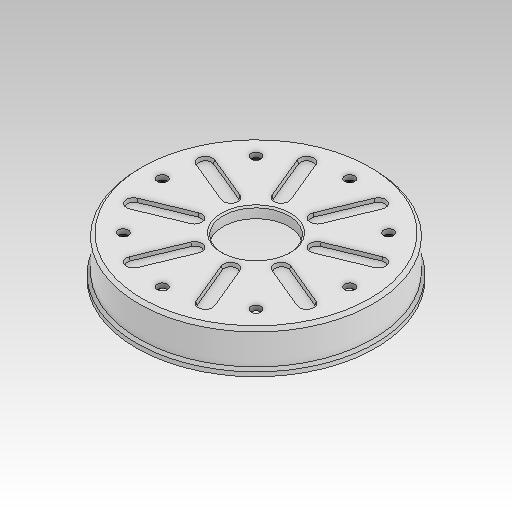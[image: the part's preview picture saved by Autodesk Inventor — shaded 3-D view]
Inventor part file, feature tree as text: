
AUTODESK INVENTOR PART (.ipt)
format: ipt  version: 2020 (Build 240168000, 168)  size: 1,618,944 bytes
history: native  units: mm
features: other x11, extrude x6, sketch x6, pattern_circular x4, chamfer x2, fillet x2, revolve x1, imported_body x1
ambient origin geometry x8: Origin, YZ Plane, XZ Plane, XY Plane, X Axis, Y Axis, Z Axis, Center Point
bodies: Solid1 (feature_tree)
feature tree (33):
  other  "HD_mastersketch.ipt"
  other  "Blocks"
  revolve  "Revolution1"  [1 undecoded]
  extrude  "Extrusion1"  Depth=4.0mm TaperAngle=0.0deg
  extrude  "Extrusion3"  Depth=1.7mm
  pattern_circular  "Circular Pattern1"  Count=73 Angle=360.0deg
  chamfer  "Chamfer1"  Distance=3.2mm
  extrude  "Extrusion2"  Depth=1.0mm
  fillet  "Fillet1"  Radius=4.0mm
  pattern_circular  "Circular Pattern2"  Angle=45.0deg  [1 undecoded]
  extrude  "Extrusion5"  Depth=10.0mm TaperAngle=0.0deg
  fillet  "Fillet2"  Radius=0.5mm
  pattern_circular  "Circular Pattern3"  Count=68 Angle=360.0deg
  extrude  "Extrusion6"  Depth=1.0mm
  chamfer  "Chamfer2"  Distance=22.5mm
  pattern_circular  "Circular Pattern4"  [2 undecoded]
  extrude  "Extrusion7"  Depth=1.0mm TaperAngle=0.0deg
  other  "608 bearing"
  other  "Belt"
  other  "Rotor"
  imported_body  "Base"
  sketch  "Sketch5"  dims[d0=10.0mm d24=7.0mm d25=22.0mm d26=8.0mm]
  sketch  "Sketch6"  dims[d1=90.0deg d4=4.0mm d5=0.0mm]
  sketch  "Sketch7"  dims[d6=80.0mm d7=360.0deg d9=1.7mm]
  other  "M3NutDepth_bot"
  other  "BeltCutDepth_bot"
  other  "M3NutDepth_top"
  other  "BeltCutDepth_top"
  sketch  "Sketch10"  dims[d11=1.25mm]
  sketch  "Sketch11"  dims[d12=4.0mm d13=0.0mm]
  sketch  "Sketch12"  dims[d14=0.5mm d15=730.0mm d16=360.0deg d18=3.2mm d19=5.7mm d20=4.0mm d21=0.0mm d34=0.5mm d35=2.0mm d36=45.0deg d37=0.8mm d38=1.8mm d39=8.726646mm d40=0.523599mm d41=0.523599mm d42=0.523599mm d43=0.523599mm d44=0.523599mm d45=2.792527mm d46=0.523599mm d47=68.0mm d48=70.740362mm d49=1.780032mm d50=9.749343mm d51=7.969311mm d52=6.189278mm d53=4.409246mm d54=2.629213mm d55=0.523599mm d56=0.523599mm d57=0.523599mm d58=0.523599mm d59=0.523599mm d60=11.529376mm d61=13.309408mm d62=15.089441mm d63=16.869473mm d64=18.649506mm d65=0.523599mm d66=0.523599mm d67=20.429538mm d68=22.209571mm d69=0.243598mm d70=72.932651mm d71=10.0mm d72=0.0mm d73=0.5mm d74=680.0mm d75=360.0deg d78=15.0mm d79=22.5mm d80=2.0mm d81=1.0mm d82=0.0mm d83=0.3mm d84=1.0mm d85=45.0deg d86=80.0mm d87=360.0deg d89=10.0mm d90=0.0mm d91=1.0mm d92=0.5mm d93=0.872665mm d94=0.5mm d95=0.872665mm]
  other  "608 bearing:1"
  other  "608 bearing:2"
note: 4 required parameter values undecoded (feature->parameter linkage not recoverable at this tier; creation-order binding heuristic only, values carry confidence <= 0.55)